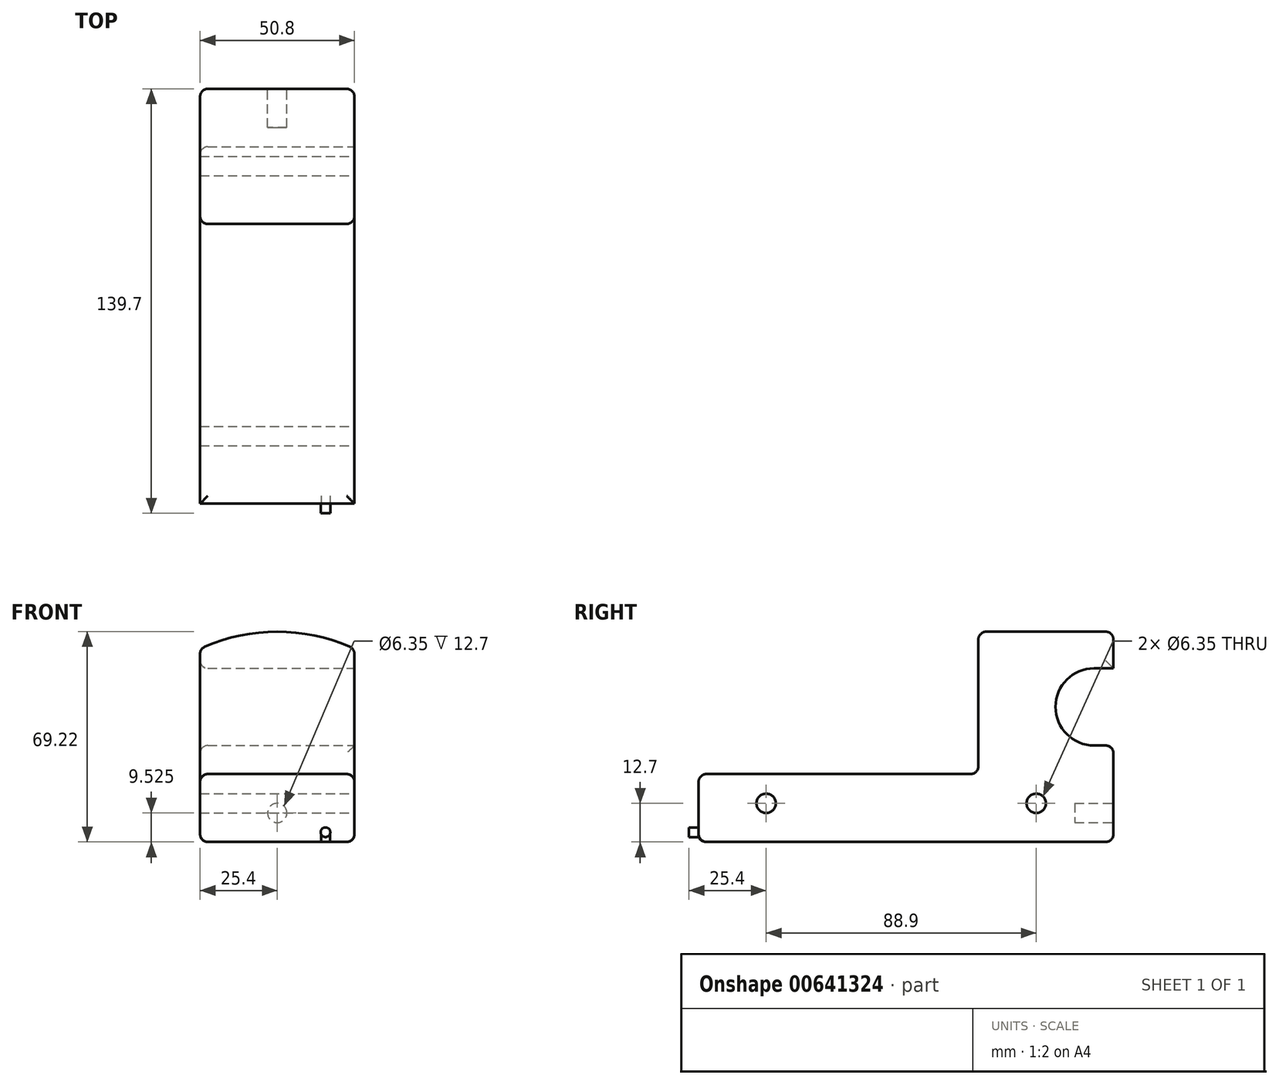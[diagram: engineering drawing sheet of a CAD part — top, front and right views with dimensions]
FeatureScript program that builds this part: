
annotation { "Feature Type Name" : "Feature", "Feature Type Description" : "" }
export const myFeature = defineFeature(function(context is Context, id is Id, definition is map)
    precondition{}
    {
        {
            var Q0;
            Q0=qCreatedBy(makeId("Front.planeOp"),FACE);
            var sketch = newSketch(context, id + "F0", { "sketchPlane" : qUnion([Q0])});
            skLineSegment(sketch, "E0", {"start": v(0, 0) * mm, "end": v(50.8, 0) * mm});
            skLineSegment(sketch, "E1", {"start": v(50.8, 0) * mm, "end": v(50.8, 22.35) * mm});
            skLineSegment(sketch, "E2", {"start": v(25.4, 0) * mm, "end": v(25.4, 35.05) * mm});
            skCircle(sketch, "E3", {"center": v(25.4, 35.05) * mm, "radius": 19.05 * mm});
            skLineSegment(sketch, "E4", {"start": v(50.8, 22.35) * mm, "end": v(0, 22.35) * mm});
            skLineSegment(sketch, "E5", {"start": v(0, 22.35) * mm, "end": v(0, 0) * mm});
            skSolve(sketch);
        }
        {
            var Q0;
            {var subQ0=sQuery(id+"F0.wireOp",EDGE,"E5");Q0=makeQuery(id+"F0.imprint","IMPRINT",FACE,{"disambiguationData":[TD([[makeQuery(id+"F0.imprint","IMPRINT",EDGE,{"derivedFrom":subQ0}),1.0]])]});}
            var Q1;
            {var subQ0=sQuery(id+"F0.wireOp",EDGE,"E4");var subQ1=sQuery(id+"F0.wireOp",EDGE,"E3");var subQ2=makeQuery(id+"F0.imprint","INTERSECT",VERTEX,{"disambiguationData":[OD(0.0)],"derivedFrom":[subQ1,subQ0]});Q1=makeQuery(id+"F0.imprint","IMPRINT",FACE,{"disambiguationData":[TD([[makeQuery(id+"F0.imprint","IMPRINT",EDGE,{"disambiguationData":[TD([[subQ2,1.0]])],"derivedFrom":subQ1}),1.0]])]});}
            var Q2;
            {var subQ0=sQuery(id+"F0.wireOp",EDGE,"E4");var subQ1=sQuery(id+"F0.wireOp",EDGE,"E2");var subQ2=makeQuery(id+"F0.imprint","INTERSECT",VERTEX,{"derivedFrom":[subQ1,subQ0]});Q2=makeQuery(id+"F0.imprint","IMPRINT",FACE,{"disambiguationData":[TD([[makeQuery(id+"F0.imprint","IMPRINT",EDGE,{"disambiguationData":[TD([[subQ2,1.0]])],"derivedFrom":subQ1}),1.0]])]});}
            var Q3;
            {var subQ0=sQuery(id+"F0.wireOp",EDGE,"E4");var subQ1=sQuery(id+"F0.wireOp",EDGE,"E2");var subQ2=makeQuery(id+"F0.imprint","INTERSECT",VERTEX,{"derivedFrom":[subQ1,subQ0]});Q3=makeQuery(id+"F0.imprint","IMPRINT",FACE,{"disambiguationData":[TD([[makeQuery(id+"F0.imprint","IMPRINT",EDGE,{"disambiguationData":[TD([[subQ2,1.0]])],"derivedFrom":subQ1}),-1.0]])]});}
            var Q4;
            {var subQ5=sQuery(id+"F0.wireOp",EDGE,"E1");Q4=makeQuery(id+"F0.imprint","IMPRINT",FACE,{"disambiguationData":[TD([[makeQuery(id+"F0.imprint","IMPRINT",EDGE,{"derivedFrom":subQ5}),1.0]])]});}
            extrude(context, id + "F1", {"entities" : qUnion([Q0, Q1, Q2, Q3, Q4]), "depth" : 95.25 * mm, "offsetDistance" : 25.4 * mm});
        }
        {
            var Q0;
            Q0=makeQuery(id+"F1.opExtrude","CAP_FACE",FACE,{"disambiguationData":[OSD([sQuery(id+"F0.wireOp",EDGE,"E0"),sQuery(id+"F0.wireOp",EDGE,"E1"),sQuery(id+"F0.wireOp",EDGE,"E3"),sQuery(id+"F0.wireOp",EDGE,"E4"),sQuery(id+"F0.wireOp",EDGE,"E5")])],"isStart":true});
            var sketch = newSketch(context, id + "F2", { "sketchPlane" : qUnion([Q0])});
            skLineSegment(sketch, "E6", {"start": v(-25.4, 0) * mm, "end": v(-25.4, 9.52) * mm});
            skArc(sketch, "E7", {"start": v(-58.24, 59.37) * mm, "mid": v(-16.33, 68.52) * mm, "end": v(20.9, 47.2) * mm});
            skLineSegment(sketch, "E8", {"start": v(0, 22.35) * mm, "end": v(0, 63.54) * mm});
            skLineSegment(sketch, "E9", {"start": v(-50.8, 22.35) * mm, "end": v(-50.8, 63.54) * mm});
            skSolve(sketch);
        }
        {
            var Q0;
            Q0 = qSketchRegion(id + "F2", true);
            var Q1;
            {var subQ3=sQuery(id+"F0.wireOp",EDGE,"E1");var subQ4=makeQuery(id+"F1.opExtrude","CAP_EDGE",EDGE,{"disambiguationData":[OSD([subQ3])],"isStart":true});Q1=makeQuery(id+"F2.imprint","IMPRINT",FACE,{"disambiguationData":[TD([[makeQuery(id+"F2.imprint","IMPRINT",EDGE,{"derivedFrom":subQ4}),-1.0]])]});}
            var Q2;
            {var subQ2=sQuery(id+"F2.wireOp",EDGE,"E8");Q2=makeQuery(id+"F2.imprint","IMPRINT",FACE,{"disambiguationData":[TD([[makeQuery(id+"F2.imprint","IMPRINT",EDGE,{"derivedFrom":subQ2}),1.0]])]});}
            extrude(context, id + "F3", {"entities" : qUnion([Q0, Q1, Q2]), "operationType" : NewBodyOperationType.ADD, "depth" : 44.45 * mm, "offsetDistance" : 25.4 * mm});
        }
        {
            var Q0;
            {var subQ0=sQuery(id+"F0.wireOp",EDGE,"E1");Q0=makeQuery(id+"F3.boolean.opBoolean","MERGE",FACE,{"derivedFrom":[makeQuery(id+"F1.opExtrude","SWEPT_FACE",FACE,{"disambiguationData":[OSD([subQ0])]}),makeQuery(id+"F3.opExtrude","SWEPT_FACE",FACE,{"disambiguationData":[OSD([subQ0,sQuery(id+"F2.wireOp",EDGE,"E9")])]})]});}
            var sketch = newSketch(context, id + "F4", { "sketchPlane" : qUnion([Q0])});
            skLineSegment(sketch, "E10", {"start": v(44.45, 0) * mm, "end": v(44.45, 44.45) * mm});
            skLineSegment(sketch, "E11", {"start": v(44.45, 44.45) * mm, "end": v(38.1, 44.45) * mm});
            skCircle(sketch, "E12", {"center": v(38.1, 44.45) * mm, "radius": 12.7 * mm});
            skLineSegment(sketch, "E13", {"start": v(38.1, 57.15) * mm, "end": v(44.45, 57.15) * mm});
            skLineSegment(sketch, "E14", {"start": v(38.1, 31.75) * mm, "end": v(44.45, 31.75) * mm});
            skSolve(sketch);
        }
        {
            var Q0;
            {var subQ0=sQuery(id+"F4.wireOp",EDGE,"E14");Q0=makeQuery(id+"F4.imprint","IMPRINT",FACE,{"disambiguationData":[TD([[makeQuery(id+"F4.imprint","IMPRINT",EDGE,{"derivedFrom":subQ0}),1.0]])]});}
            var Q1;
            {var subQ0=sQuery(id+"F4.wireOp",EDGE,"E12");var subQ7=makeQuery(id+"F4.imprint","INTERSECT",VERTEX,{"derivedFrom":[subQ0,sQuery(id+"F4.wireOp",EDGE,"E13")]});Q1=makeQuery(id+"F4.imprint","IMPRINT",FACE,{"disambiguationData":[TD([[makeQuery(id+"F4.imprint","IMPRINT",EDGE,{"disambiguationData":[TD([[subQ7,-1.0]])],"derivedFrom":subQ0}),1.0]])]});}
            var Q2;
            {var subQ0=sQuery(id+"F4.wireOp",EDGE,"E13");Q2=makeQuery(id+"F4.imprint","IMPRINT",FACE,{"disambiguationData":[TD([[makeQuery(id+"F4.imprint","IMPRINT",EDGE,{"derivedFrom":subQ0}),-1.0]])]});}
            extrude(context, id + "F5", {"entities" : qUnion([Q0, Q1, Q2]), "operationType" : NewBodyOperationType.REMOVE, "endBound" : BoundingType.THROUGH_ALL, "oppositeDirection" : true, "depth" : 25.4 * mm, "offsetDistance" : 25.4 * mm});
        }
        {
            var Q0;
            {var subQ0=sQuery(id+"F0.wireOp",EDGE,"E1");Q0=makeQuery(id+"F3.boolean.opBoolean","MERGE",FACE,{"derivedFrom":[makeQuery(id+"F1.opExtrude","SWEPT_FACE",FACE,{"disambiguationData":[OSD([subQ0])]}),makeQuery(id+"F3.opExtrude","SWEPT_FACE",FACE,{"disambiguationData":[OSD([subQ0,sQuery(id+"F2.wireOp",EDGE,"E9")])]})]});}
            var sketch = newSketch(context, id + "F6", { "sketchPlane" : qUnion([Q0])});
            skLineSegment(sketch, "E15", {"start": v(44.45, 0) * mm, "end": v(44.45, 12.7) * mm});
            skLineSegment(sketch, "E16", {"start": v(44.45, 12.7) * mm, "end": v(19.05, 12.7) * mm});
            skCircle(sketch, "E17", {"center": v(19.05, 12.7) * mm, "radius": 3.18 * mm});
            skLineSegment(sketch, "E18", {"start": v(19.05, 12.7) * mm, "end": v(-37.64, 12.7) * mm});
            skLineSegment(sketch, "E19", {"start": v(44.45, 12.7) * mm, "end": v(-69.85, 12.7) * mm});
            skCircle(sketch, "E20", {"center": v(-69.85, 12.7) * mm, "radius": 3.18 * mm});
            skSolve(sketch);
        }
        {
            var Q0;
            {var subQ0=sQuery(id+"F6.wireOp",EDGE,"E19");var subQ1=sQuery(id+"F6.wireOp",EDGE,"E17");var subQ2=makeQuery(id+"F6.imprint","INTERSECT",VERTEX,{"disambiguationData":[OD(0.0)],"derivedFrom":[subQ1,subQ0]});Q0=makeQuery(id+"F6.imprint","IMPRINT",FACE,{"disambiguationData":[TD([[makeQuery(id+"F6.imprint","IMPRINT",EDGE,{"disambiguationData":[TD([[subQ2,1.0]])],"derivedFrom":subQ1}),1.0]])]});}
            var Q1;
            Q1=makeQuery(id+"F6.imprint","IMPRINT",FACE,{"disambiguationData":[TD([[makeQuery(id+"F6.imprint","IMPRINT",EDGE,{"derivedFrom":sQuery(id+"F6.wireOp",EDGE,"E20")}),1.0]])]});
            var Q2;
            {var subQ0=sQuery(id+"F6.wireOp",EDGE,"E19");var subQ1=sQuery(id+"F6.wireOp",EDGE,"E17");var subQ2=makeQuery(id+"F6.imprint","INTERSECT",VERTEX,{"disambiguationData":[OD(0.0)],"derivedFrom":[subQ1,subQ0]});Q2=makeQuery(id+"F6.imprint","IMPRINT",FACE,{"disambiguationData":[TD([[makeQuery(id+"F6.imprint","IMPRINT",EDGE,{"disambiguationData":[TD([[subQ2,-1.0]])],"derivedFrom":subQ1}),1.0]])]});}
            extrude(context, id + "F7", {"entities" : qUnion([Q0, Q1, Q2]), "operationType" : NewBodyOperationType.REMOVE, "endBound" : BoundingType.THROUGH_ALL, "oppositeDirection" : true, "depth" : 25.4 * mm, "offsetDistance" : 25.4 * mm});
        }
        {
            var Q0;
            {var subQ0=sQuery(id+"F2.wireOp",EDGE,"E8");var subQ1=sQuery(id+"F0.wireOp",EDGE,"E5");var subQ2=sQuery(id+"F0.wireOp",EDGE,"E1");var subQ3=sQuery(id+"F0.wireOp",EDGE,"E0");var subQ4=sQuery(id+"F2.wireOp",EDGE,"E9");Q0=makeQuery(id+"F5.boolean.opBoolean","SPLIT",FACE,{"disambiguationData":[TD([makeQuery(id+"F1.opExtrude","SWEPT_FACE",FACE,{"disambiguationData":[OSD([subQ3])]})])],"derivedFrom":makeQuery(id+"F3.opExtrude","CAP_FACE",FACE,{"disambiguationData":[OSD([subQ3,subQ2,subQ1,sQuery(id+"F2.wireOp",EDGE,"E7"),subQ0,subQ4])],"isStart":false})});}
            var sketch = newSketch(context, id + "F8", { "sketchPlane" : qUnion([Q0])});
            skLineSegment(sketch, "E21", {"start": v(0, 0) * mm, "end": v(0, 9.53) * mm});
            skLineSegment(sketch, "E22", {"start": v(0, 9.53) * mm, "end": v(-25.4, 9.53) * mm});
            skCircle(sketch, "E23", {"center": v(-25.4, 9.53) * mm, "radius": 3.18 * mm});
            skSolve(sketch);
        }
        {
            var Q0;
            Q0=makeQuery(id+"F8.imprint","IMPRINT",FACE,{"disambiguationData":[TD([[makeQuery(id+"F8.imprint","IMPRINT",EDGE,{"derivedFrom":sQuery(id+"F8.wireOp",EDGE,"E23")}),1.0]])]});
            extrude(context, id + "F9", {"entities" : qUnion([Q0]), "operationType" : NewBodyOperationType.REMOVE, "oppositeDirection" : true, "depth" : 12.7 * mm, "offsetDistance" : 25.4 * mm});
        }
        {
            var Q0;
            Q0=qCreatedBy(makeId("Top.planeOp"),FACE);
            cPlane(context, id + "F10", {"entities" : qUnion([Q0]), "cplaneType" : CPlaneType.OFFSET, "offset" : 54.1 * mm, "width" : 152.4 * mm, "height" : 152.4 * mm});
        }
        {
            var Q0;
            Q0=qCreatedBy(id+"F10.planeOp",FACE);
            var sketch = newSketch(context, id + "F11", { "sketchPlane" : qUnion([Q0])});
            skPoint(sketch, "E24.0", {"position": v(25.4, -95.25) * mm});
            skLineSegment(sketch, "E25", {"start": v(44.45, 0) * mm, "end": v(44.45, -95.25) * mm});
            skLineSegment(sketch, "E26", {"start": v(6.35, -95.25) * mm, "end": v(6.35, 0) * mm});
            skLineSegment(sketch, "E27", {"start": v(25.4, -95.25) * mm, "end": v(25.4, -72.9) * mm});
            skCircle(sketch, "E28", {"center": v(25.4, -72.9) * mm, "radius": 6.35 * mm});
            skSolve(sketch);
        }
        {
            var Q0;
            Q0=makeQuery(id+"F11.imprint","IMPRINT",FACE,{"disambiguationData":[TD([[makeQuery(id+"F11.imprint","IMPRINT",EDGE,{"derivedFrom":sQuery(id+"F11.wireOp",EDGE,"E28")}),1.0]])]});
            extrude(context, id + "F12", {"entities" : qUnion([Q0]), "operationType" : NewBodyOperationType.REMOVE, "oppositeDirection" : true, "depth" : 6.35 * mm, "offsetDistance" : 25.4 * mm});
        }
        {
            var Q0;
            Q0=makeQuery(id+"F1.opExtrude","CAP_FACE",FACE,{"disambiguationData":[OSD([sQuery(id+"F0.wireOp",EDGE,"E0"),sQuery(id+"F0.wireOp",EDGE,"E1"),sQuery(id+"F0.wireOp",EDGE,"E3"),sQuery(id+"F0.wireOp",EDGE,"E4"),sQuery(id+"F0.wireOp",EDGE,"E5")])],"isStart":false});
            var sketch = newSketch(context, id + "F13", { "sketchPlane" : qUnion([Q0])});
            skLineSegment(sketch, "E29", {"start": v(0, 0) * mm, "end": v(0, 3.18) * mm});
            skLineSegment(sketch, "E30", {"start": v(0, 3.18) * mm, "end": v(9.53, 3.18) * mm});
            skCircle(sketch, "E31", {"center": v(9.53, 3.18) * mm, "radius": 1.59 * mm});
            skLineSegment(sketch, "E32", {"start": v(25.4, 0) * mm, "end": v(25.4, 15.88) * mm});
            skCircle(sketch, "E33.MirrorC", {"center": v(41.28, 3.18) * mm, "radius": 1.59 * mm});
            skCircle(sketch, "E34", {"center": v(25.4, 15.88) * mm, "radius": 1.59 * mm});
            skSolve(sketch);
        }
        {
            var Q0;
            Q0=makeQuery(id+"F13.imprint","IMPRINT",FACE,{"disambiguationData":[TD([[makeQuery(id+"F13.imprint","IMPRINT",EDGE,{"derivedFrom":sQuery(id+"F13.wireOp",EDGE,"E34")}),1.0]])]});
            var Q1;
            Q1=makeQuery(id+"F13.imprint","IMPRINT",FACE,{"disambiguationData":[TD([[makeQuery(id+"F13.imprint","IMPRINT",EDGE,{"derivedFrom":sQuery(id+"F13.wireOp",EDGE,"E33.MirrorC")}),-1.0]])]});
            var Q2;
            Q2=makeQuery(id+"F13.imprint","IMPRINT",FACE,{"disambiguationData":[TD([[makeQuery(id+"F13.imprint","IMPRINT",EDGE,{"derivedFrom":sQuery(id+"F13.wireOp",EDGE,"E31")}),1.0]])]});
            extrude(context, id + "F14", {"entities" : qUnion([Q0, Q1, Q2]), "operationType" : NewBodyOperationType.REMOVE, "oppositeDirection" : true, "depth" : 3.17 * mm, "offsetDistance" : 25.4 * mm});
        }
        {
            var Q0;
            {var subQ0=sQuery(id+"F0.wireOp",EDGE,"E5");var subQ1=sQuery(id+"F0.wireOp",EDGE,"E0");Q0=makeQuery(id+"F3.boolean.opBoolean","MERGE",EDGE,{"derivedFrom":[makeQuery(id+"F1.opExtrude","SWEPT_EDGE",EDGE,{"disambiguationData":[OSD([subQ1,subQ0])]}),makeQuery(id+"F3.opExtrude","SWEPT_EDGE",EDGE,{"disambiguationData":[OSD([subQ1,subQ0])]})]});}
            var Q1;
            Q1=makeQuery(id+"F5.boolean.opBoolean","COPY",EDGE,{"derivedFrom":makeQuery(id+"F5.opExtrude","SWEPT_EDGE",EDGE,{"disambiguationData":[OSD([sQuery(id+"F0.wireOp",EDGE,"E1"),sQuery(id+"F2.wireOp",EDGE,"E9"),sQuery(id+"F4.wireOp",EDGE,"E13")])]})});
            var Q2;
            Q2=makeQuery(id+"F5.boolean.opBoolean","COPY",EDGE,{"derivedFrom":makeQuery(id+"F5.opExtrude","SWEPT_EDGE",EDGE,{"disambiguationData":[OSD([sQuery(id+"F4.wireOp",EDGE,"E10"),sQuery(id+"F4.wireOp",EDGE,"E14")])]})});
            var Q3;
            Q3=makeQuery(id+"F5.boolean.opBoolean","COPY",EDGE,{"derivedFrom":makeQuery(id+"F5.opExtrude","CAP_EDGE",EDGE,{"disambiguationData":[OSD([sQuery(id+"F4.wireOp",EDGE,"E13")])],"isStart":true})});
            var Q4;
            Q4=makeQuery(id+"F5.boolean.opBoolean","COPY",EDGE,{"derivedFrom":makeQuery(id+"F5.opExtrude","CAP_EDGE",EDGE,{"disambiguationData":[OSD([sQuery(id+"F4.wireOp",EDGE,"E12")])],"isStart":true})});
            var Q5;
            {var subQ0=sQuery(id+"F0.wireOp",EDGE,"E5");Q5=makeQuery(id+"F5.boolean.opBoolean","INTERSECT",EDGE,{"derivedFrom":[makeQuery(id+"F3.boolean.opBoolean","MERGE",FACE,{"derivedFrom":[makeQuery(id+"F1.opExtrude","SWEPT_FACE",FACE,{"disambiguationData":[OSD([subQ0])]}),makeQuery(id+"F3.opExtrude","SWEPT_FACE",FACE,{"disambiguationData":[OSD([subQ0,sQuery(id+"F2.wireOp",EDGE,"E8")])]})]}),makeQuery(id+"F5.opExtrude","SWEPT_FACE",FACE,{"disambiguationData":[OSD([sQuery(id+"F4.wireOp",EDGE,"E12")])]})]});}
            var Q6;
            Q6=makeQuery(id+"F3.opExtrude","CAP_EDGE",EDGE,{"disambiguationData":[OSD([sQuery(id+"F0.wireOp",EDGE,"E5"),sQuery(id+"F2.wireOp",EDGE,"E8")])],"isStart":true});
            var Q7;
            Q7=makeQuery(id+"F3.opExtrude","CAP_EDGE",EDGE,{"disambiguationData":[OSD([sQuery(id+"F0.wireOp",EDGE,"E1"),sQuery(id+"F2.wireOp",EDGE,"E9")])],"isStart":true});
            var Q8;
            Q8=makeQuery(id+"F1.opExtrude","SWEPT_EDGE",EDGE,{"disambiguationData":[OSD([sQuery(id+"F0.wireOp",EDGE,"E1"),sQuery(id+"F0.wireOp",EDGE,"E4")])]});
            var Q9;
            {var subQ0=sQuery(id+"F0.wireOp",EDGE,"E4");Q9=makeQuery(id+"F1.opExtrude","SWEPT_FACE",FACE,{"disambiguationData":[OSD([subQ0]),TDD([makeQuery(id+"F0.imprint","IMPRINT",EDGE,{"disambiguationData":[TD([[makeQuery(id+"F0.imprint","INTERSECT",VERTEX,{"derivedFrom":[subQ0,sQuery(id+"F0.wireOp",EDGE,"E5")]}),1.0]])],"derivedFrom":subQ0})])]});}
            var Q10;
            {var subQ0=sQuery(id+"F0.wireOp",EDGE,"E4");Q10=makeQuery(id+"F1.opExtrude","SWEPT_FACE",FACE,{"disambiguationData":[OSD([subQ0]),TDD([makeQuery(id+"F0.imprint","IMPRINT",EDGE,{"disambiguationData":[TD([[makeQuery(id+"F0.imprint","INTERSECT",VERTEX,{"derivedFrom":[sQuery(id+"F0.wireOp",EDGE,"E1"),subQ0]}),-1.0]])],"derivedFrom":subQ0})])]});}
            var Q11;
            Q11=makeQuery(id+"F3.opExtrude","CAP_FACE",FACE,{"disambiguationData":[OSD([sQuery(id+"F0.wireOp",EDGE,"E0"),sQuery(id+"F0.wireOp",EDGE,"E1"),sQuery(id+"F0.wireOp",EDGE,"E5"),sQuery(id+"F2.wireOp",EDGE,"E7"),sQuery(id+"F2.wireOp",EDGE,"E8"),sQuery(id+"F2.wireOp",EDGE,"E9")])],"isStart":true});
            var Q12;
            Q12=makeQuery(id+"F3.opExtrude","CAP_EDGE",EDGE,{"disambiguationData":[OSD([sQuery(id+"F0.wireOp",EDGE,"E0")])],"isStart":false});
            var Q13;
            {var subQ0=sQuery(id+"F2.wireOp",EDGE,"E8");var subQ1=sQuery(id+"F0.wireOp",EDGE,"E5");var subQ2=sQuery(id+"F0.wireOp",EDGE,"E0");Q13=makeQuery(id+"F5.boolean.opBoolean","SPLIT",EDGE,{"disambiguationData":[TD([makeQuery(id+"F1.opExtrude","SWEPT_FACE",FACE,{"disambiguationData":[OSD([subQ2])]})])],"derivedFrom":makeQuery(id+"F3.opExtrude","CAP_EDGE",EDGE,{"disambiguationData":[OSD([subQ1,subQ0])],"isStart":false})});}
            var Q14;
            Q14=makeQuery(id+"F1.opExtrude","CAP_EDGE",EDGE,{"disambiguationData":[OSD([sQuery(id+"F0.wireOp",EDGE,"E5")])],"isStart":false});
            var Q15;
            Q15=makeQuery(id+"F1.opExtrude","CAP_EDGE",EDGE,{"disambiguationData":[OSD([sQuery(id+"F0.wireOp",EDGE,"E1")])],"isStart":false});
            var Q16;
            {var subQ0=sQuery(id+"F0.wireOp",EDGE,"E0");Q16=makeQuery(id+"F3.boolean.opBoolean","MERGE",FACE,{"derivedFrom":[makeQuery(id+"F1.opExtrude","SWEPT_FACE",FACE,{"disambiguationData":[OSD([subQ0])]}),makeQuery(id+"F3.opExtrude","SWEPT_FACE",FACE,{"disambiguationData":[OSD([subQ0])]})]});}
            var Q17;
            {var subQ0=sQuery(id+"F2.wireOp",EDGE,"E9");var subQ1=sQuery(id+"F0.wireOp",EDGE,"E1");var subQ2=sQuery(id+"F0.wireOp",EDGE,"E0");Q17=makeQuery(id+"F5.boolean.opBoolean","SPLIT",EDGE,{"disambiguationData":[TD([makeQuery(id+"F1.opExtrude","SWEPT_FACE",FACE,{"disambiguationData":[OSD([subQ2])]})])],"derivedFrom":makeQuery(id+"F3.opExtrude","CAP_EDGE",EDGE,{"disambiguationData":[OSD([subQ1,subQ0])],"isStart":false})});}
            var Q18;
            {var subQ0=sQuery(id+"F2.wireOp",EDGE,"E9");var subQ1=sQuery(id+"F0.wireOp",EDGE,"E1");var subQ2=sQuery(id+"F2.wireOp",EDGE,"E7");Q18=makeQuery(id+"F5.boolean.opBoolean","SPLIT",EDGE,{"disambiguationData":[TD([makeQuery(id+"F3.opExtrude","SWEPT_FACE",FACE,{"disambiguationData":[OSD([subQ2])]})])],"derivedFrom":makeQuery(id+"F3.opExtrude","CAP_EDGE",EDGE,{"disambiguationData":[OSD([subQ1,subQ0])],"isStart":false})});}
            var Q19;
            Q19=makeQuery(id+"F3.opExtrude","SWEPT_FACE",FACE,{"disambiguationData":[OSD([sQuery(id+"F2.wireOp",EDGE,"E7")])]});
            var Q20;
            {var subQ0=sQuery(id+"F2.wireOp",EDGE,"E8");var subQ1=sQuery(id+"F0.wireOp",EDGE,"E5");var subQ2=sQuery(id+"F2.wireOp",EDGE,"E7");Q20=makeQuery(id+"F5.boolean.opBoolean","SPLIT",EDGE,{"disambiguationData":[TD([makeQuery(id+"F3.opExtrude","SWEPT_FACE",FACE,{"disambiguationData":[OSD([subQ2])]})])],"derivedFrom":makeQuery(id+"F3.opExtrude","CAP_EDGE",EDGE,{"disambiguationData":[OSD([subQ1,subQ0])],"isStart":false})});}
            fillet(context, id + "F15", {"entities" : qUnion([Q0, Q1, Q2, Q3, Q4, Q5, Q6, Q7, Q8, Q9, Q10, Q11, Q12, Q13, Q14, Q15, Q16, Q17, Q18, Q19, Q20]), "radius" : 2.54 * mm, "tangentPropagation" : true, "allowEdgeOverflow" : false});
        }
    });
